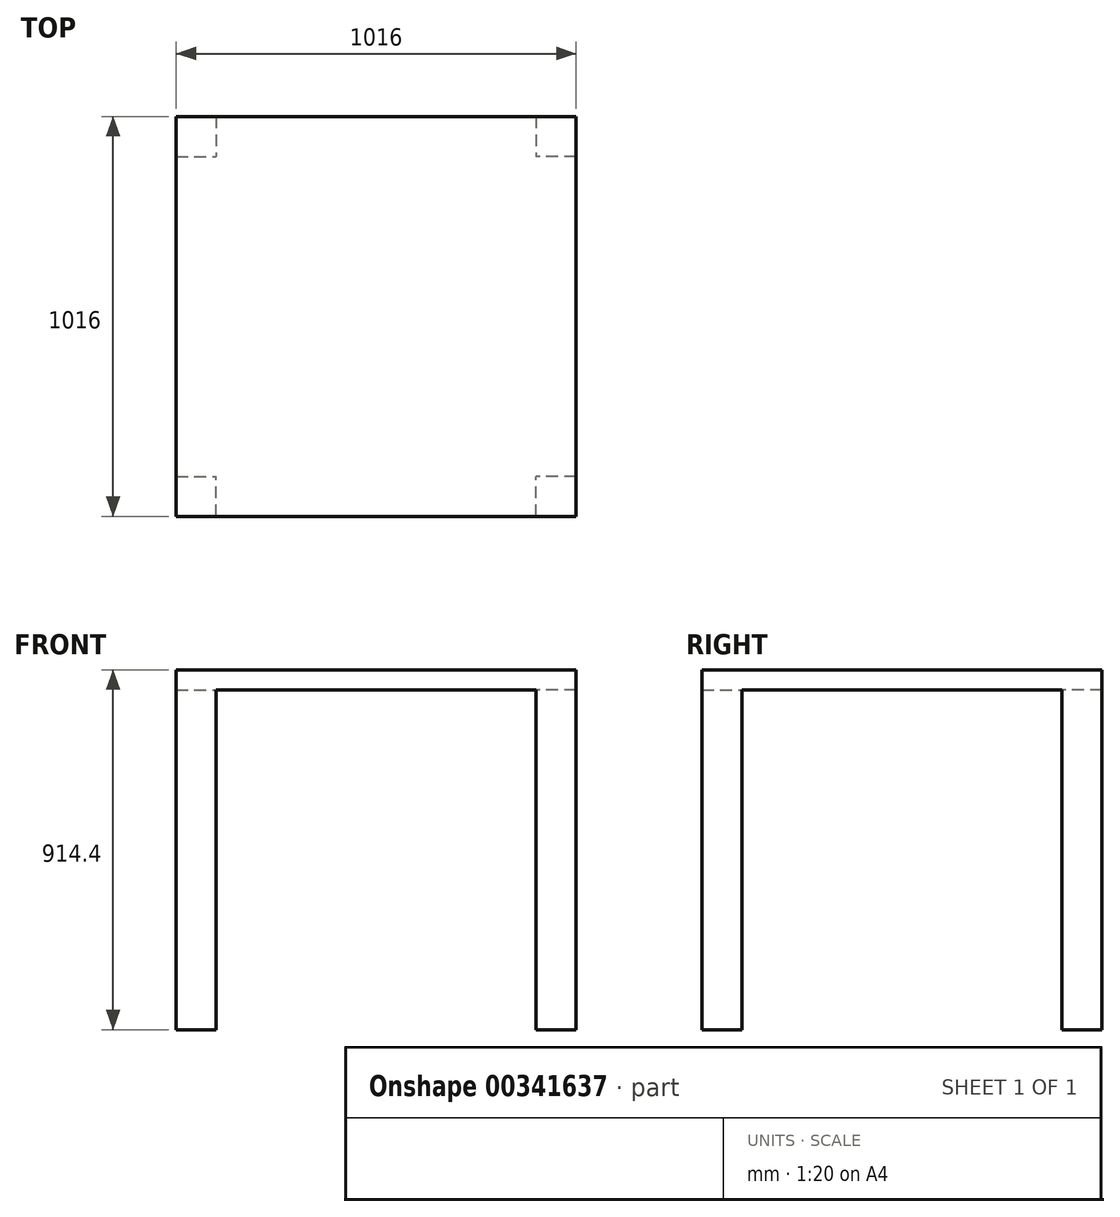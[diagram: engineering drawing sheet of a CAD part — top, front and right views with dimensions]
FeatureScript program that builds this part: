
annotation { "Feature Type Name" : "Feature", "Feature Type Description" : "" }
export const myFeature = defineFeature(function(context is Context, id is Id, definition is map)
    precondition{}
    {
        {
            var Q0;
            Q0=qCreatedBy(makeId("Top.planeOp"),FACE);
            var sketch = newSketch(context, id + "F0", { "sketchPlane" : qUnion([Q0])});
            skLineSegment(sketch, "E0.bottom", {"start": v(-603.36, 539.77) * mm, "end": v(412.64, 539.77) * mm});
            skLineSegment(sketch, "E0.top", {"start": v(-603.36, -476.23) * mm, "end": v(412.64, -476.23) * mm});
            skLineSegment(sketch, "E0.left", {"start": v(-603.36, 539.77) * mm, "end": v(-603.36, -476.23) * mm});
            skLineSegment(sketch, "E0.right", {"start": v(412.64, 539.77) * mm, "end": v(412.64, -476.23) * mm});
            skSolve(sketch);
        }
        {
            var Q0;
            Q0=qSketchRegion(id+"F0",true);
            extrude(context, id + "F1", {"entities" : qUnion([Q0]), "depth" : 50.8 * mm});
        }
        {
            var Q0;
            Q0=makeQuery(id+"F1.opExtrude","CAP_FACE",FACE,{"disambiguationData":[OSD([sQuery(id+"F0.wireOp",EDGE,"E0.bottom"),sQuery(id+"F0.wireOp",EDGE,"E0.top"),sQuery(id+"F0.wireOp",EDGE,"E0.left"),sQuery(id+"F0.wireOp",EDGE,"E0.right")])],"isStart":true});
            var sketch = newSketch(context, id + "F2", { "sketchPlane" : qUnion([Q0])});
            skLineSegment(sketch, "E1.bottom", {"start": v(-603.36, 476.23) * mm, "end": v(-501.76, 476.23) * mm});
            skLineSegment(sketch, "E1.top", {"start": v(-603.36, 374.63) * mm, "end": v(-501.76, 374.63) * mm});
            skLineSegment(sketch, "E1.left", {"start": v(-603.36, 476.23) * mm, "end": v(-603.36, 374.63) * mm});
            skLineSegment(sketch, "E1.right", {"start": v(-501.76, 476.23) * mm, "end": v(-501.76, 374.63) * mm});
            skLineSegment(sketch, "E2.MirrorCS", {"start": v(311.04, 476.23) * mm, "end": v(311.04, 374.63) * mm});
            skLineSegment(sketch, "E3.MirrorCS", {"start": v(412.64, 374.63) * mm, "end": v(311.04, 374.63) * mm});
            skLineSegment(sketch, "E4.MirrorCS", {"start": v(412.64, 476.23) * mm, "end": v(412.64, 374.63) * mm});
            skLineSegment(sketch, "E5.MirrorCS", {"start": v(412.64, 476.23) * mm, "end": v(311.04, 476.23) * mm});
            skPoint(sketch, "E6.orphan", {"position": v(-567.01, 0) * mm});
            skLineSegment(sketch, "E7.MirrorCS", {"start": v(-501.76, -539.77) * mm, "end": v(-501.76, -438.17) * mm});
            skLineSegment(sketch, "E8.MirrorCS", {"start": v(-603.36, -438.17) * mm, "end": v(-501.76, -438.17) * mm});
            skLineSegment(sketch, "E9.MirrorCS", {"start": v(-603.36, -539.77) * mm, "end": v(-603.36, -438.17) * mm});
            skLineSegment(sketch, "E10.MirrorCS", {"start": v(-603.36, -539.77) * mm, "end": v(-501.76, -539.77) * mm});
            skLineSegment(sketch, "E11.MirrorCS", {"start": v(412.64, -539.77) * mm, "end": v(311.04, -539.77) * mm});
            skLineSegment(sketch, "E12.MirrorCS", {"start": v(311.04, -539.77) * mm, "end": v(311.04, -438.17) * mm});
            skLineSegment(sketch, "E13.MirrorCS", {"start": v(412.64, -438.17) * mm, "end": v(311.04, -438.17) * mm});
            skLineSegment(sketch, "E14.MirrorCS", {"start": v(412.64, -539.77) * mm, "end": v(412.64, -438.17) * mm});
            skPoint(sketch, "E15.orphan", {"position": v(-95.36, 476.23) * mm});
            skPoint(sketch, "E16.end.orphan", {"position": v(-95.36, -539.77) * mm});
            skPoint(sketch, "E16.start.orphan", {"position": v(-95.36, -31.77) * mm});
            skSolve(sketch);
        }
        {
            var Q0;
            Q0=qSketchRegion(id+"F2",true);
            extrude(context, id + "F3", {"entities" : qUnion([Q0]), "operationType" : NewBodyOperationType.ADD, "depth" : 863.6 * mm});
        }
    });
